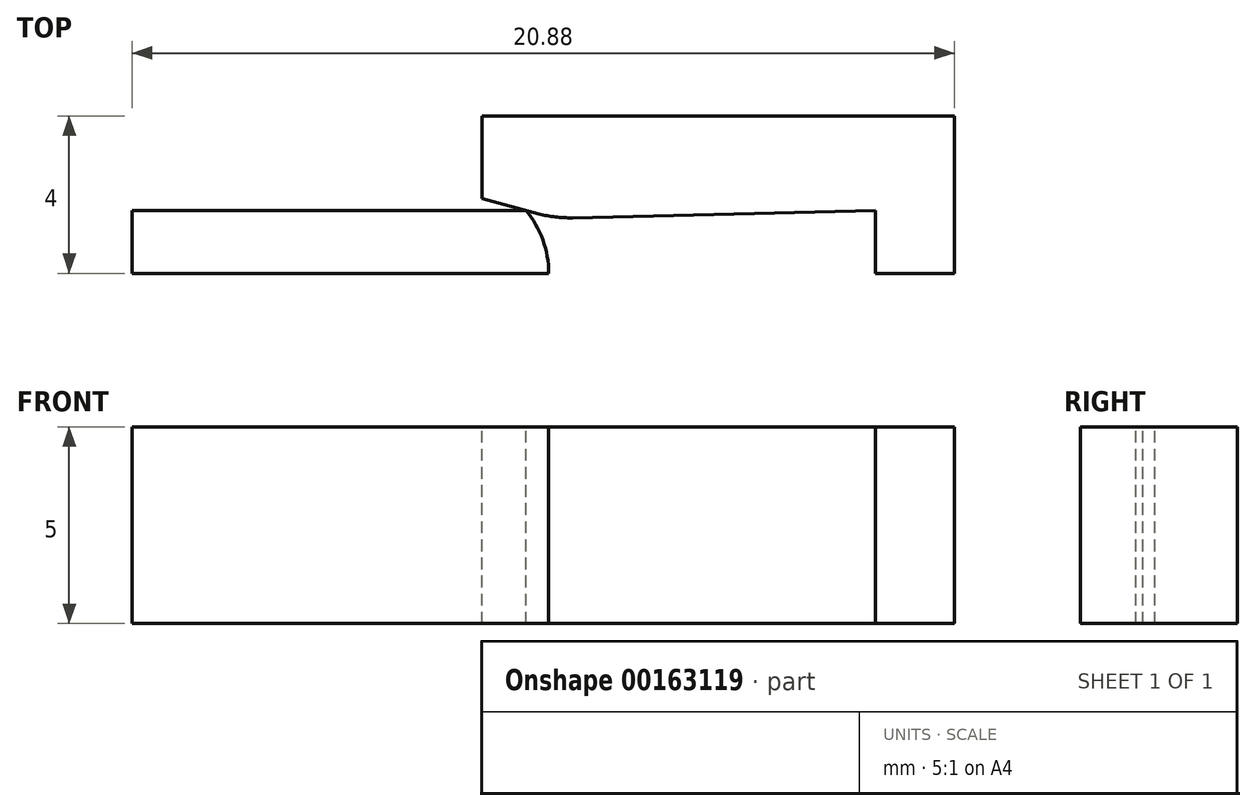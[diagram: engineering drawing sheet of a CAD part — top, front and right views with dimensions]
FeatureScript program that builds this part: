
annotation { "Feature Type Name" : "Feature", "Feature Type Description" : "" }
export const myFeature = defineFeature(function(context is Context, id is Id, definition is map)
    precondition{}
    {
        {
            var Q0;
            Q0=qCreatedBy(makeId("Top.planeOp"),FACE);
            var sketch = newSketch(context, id + "F0", { "sketchPlane" : qUnion([Q0])});
            skLineSegment(sketch, "E0", {"start": v(0, 4) * mm, "end": v(12, 4) * mm});
            skLineSegment(sketch, "E1", {"start": v(12, 4) * mm, "end": v(12, 0) * mm});
            skLineSegment(sketch, "E2", {"start": v(12, 0) * mm, "end": v(10, 0) * mm});
            skLineSegment(sketch, "E3", {"start": v(10, 0) * mm, "end": v(10, 1.6) * mm});
            skLineSegment(sketch, "E4", {"start": v(10, 1.6) * mm, "end": v(1.87, 1.4) * mm});
            skLineSegment(sketch, "E5", {"start": v(1.87, 1.4) * mm, "end": v(0, 1.9) * mm});
            skLineSegment(sketch, "E6", {"start": v(0, 1.9) * mm, "end": v(0, 4) * mm});
            skSolve(sketch);
        }
        {
            var Q0;
            Q0 = qSketchRegion(id + "F0", true);
            extrude(context, id + "F1", {"entities" : qUnion([Q0]), "oppositeDirection" : true, "depth" : 5 * mm});
        }
        {
            var Q0;
            Q0=makeQuery(id+"F1.opExtrude","SWEPT_EDGE",EDGE,{"disambiguationData":[OSD([sQuery(id+"F0.wireOp",EDGE,"E4"),sQuery(id+"F0.wireOp",EDGE,"E5")])]});
            fillet(context, id + "F2", {"entities" : qUnion([Q0]), "radius" : 3 * mm, "tangentPropagation" : true, "allowEdgeOverflow" : false});
        }
        {
            var Q0;
            Q0=qCreatedBy(makeId("Top.planeOp"),FACE);
            var sketch = newSketch(context, id + "F3", { "sketchPlane" : qUnion([Q0])});
            skLineSegment(sketch, "E7", {"start": v(1.12, 1.6) * mm, "end": v(-8.88, 1.6) * mm});
            skArc(sketch, "E8", {"start": v(1.12, 1.6) * mm, "mid": v(1.55, 0.85) * mm, "end": v(1.7, 0) * mm});
            skLineSegment(sketch, "E9", {"start": v(-8.88, 1.6) * mm, "end": v(-8.88, 0) * mm});
            skLineSegment(sketch, "E10", {"start": v(-8.88, 0) * mm, "end": v(1.7, 0) * mm});
            skSolve(sketch);
        }
        {
            var Q0;
            Q0=makeQuery(id+"F3.imprint","IMPRINT",FACE,{"disambiguationData":[TD([[makeQuery(id+"F3.imprint","IMPRINT",EDGE,{"derivedFrom":sQuery(id+"F3.wireOp",EDGE,"E7")}),1.0]])]});
            extrude(context, id + "F4", {"entities" : qUnion([Q0]), "oppositeDirection" : true, "depth" : 5 * mm});
        }
    });
